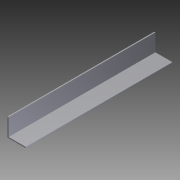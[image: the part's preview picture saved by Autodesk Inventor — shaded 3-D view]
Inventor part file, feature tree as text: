
AUTODESK INVENTOR PART (.ipt)
format: ipt  version: 2012 (Build 160160000, 160)  size: 73,728 bytes
history: native  units: in
note: dims shown in document units (in); Inventor stores cm internally (conversion verified against a paired STEP export)
features: extrude x1, sketch x1
ambient origin geometry x8: Origin, YZ Plane, XZ Plane, XY Plane, X Axis, Y Axis, Z Axis, Center Point
bodies: Solid1 (feature_tree)
feature tree (2):
  extrude  "Extrusion1"  Depth=1.0in
  sketch  "Sketch1"  dims[d0=1.0in d1=1.0in d2=0.0625in d3=0.0625in d4=8.0in d5=0.0in]
